# Revit family: ASH_Contour21_Multiproduct_S6360;S6361
name_source: partatom
category: Plumbing Fixtures
revit_build: Autodesk Revit MEP 2014 (Build: 20130308_1515(x64)
units: mm (PartAtom-declared; Revit-internal decimal feet)

## types (10) — shared parameters
AccessibilityPerformance = Part-M
Accessories = www.idealspec.co.uk
AreaUnits = millimeters
Assembly Code = C1030200
AssetType = Fixed
Brand = Armitage Shanks
ConnectionType = Plumbing
Default Elevation = 680 mm  [stored 2.23097 ft]
DurationUnit = year
ExpectedLife = 30
Finish = Chrome
IfcExportAs = IfcValveType
IfcExportType = FAUCET
InstallationInstructions = www.idealspec.co.uk/resources.html
LinearUnits = millimeters
ManufacturerURL = www.idealspec.co.uk
Material = Aluminium
NBSDescription = Support rails
NBSReference = 45-35-70/360
NominalHeight = 242 mm
NominalWidth = 107 mm
Shape = Sculptured
Size = 0 x 0 x 0 mm
Space = Internal
SpareParts = www.fastpart-spares.co.uk
URL = www.idealspec.co.uk
Uniclass2015Code = Pr_40_20_76_84
Uniclass2015Title = Support rails
Uniclass2015Version = Products v1.1
Version = 1
VolumeUnits = Litres
WarrantyDescription = Manufacturers Warranty
WarrantyDurationParts = 5
WarrantyDurationUnit = year
zero-valued in all types: CWFU, Cost, HWFU, WFU

## per-type parameters (varying)
| type | BIMObjectName | BarCode | Color | Description | Features | GrabRailMtl | Model | ModelNumber | ModelReference | Name | NettWeight | NominalLength | ProductInformation |
| S6360AC - Contour21 Support Rail 800 x 350mm - Doc M Compliant - White | ASH_ArmitageShanks_SupportRails_Contour21_S6360AC | 5017830444909 | White | Contour 21 hinged support rail 80 x 35mm diameter, doc m compliant | Hinged support rail 80 x 35mm diameter, doc m compliant | ASH_ArmitageShanks_Brassware_White_AC_Render | S6360AC | S6360AC | Contour 21 hinged support rail 80 x 35mm diameter, doc m compliant | SupportRails_Contour21_S6360AC_ArmitageShanks | 3.15 Kg | 800 mm | www.idealspec.co.uk/assets/datasheet/S6360AC |
| S6361AC - Contour21 Support Rail 650 x 350mm - NHS HTM64 - White | ASH_ArmitageShanks_SupportRails_Contour21_S6361AC | 5017830444954 | White | Contour 21 hinged support rail nhs htm64 projection 65 x 35mm diameter | Hinged support rail nhs htm64 projection 65 x 35mm diameter | ASH_ArmitageShanks_Brassware_White_AC_Render | S6361AC | S6361AC | Contour 21 hinged support rail nhs htm64 projection 65 x 35mm diameter | SupportRails_Contour21_S6361AC_ArmitageShanks | 3 Kg | 650 mm  [stored 2.13255 ft] | www.idealspec.co.uk/assets/datasheet/S6361AC |
| S636036 - Contour21 Support Rail 800 x 350mm - Doc M Compliant - Blue | ASH_ArmitageShanks_SupportRails_Contour21_S636036 | 5017830444893 | Blue | Contour 21 hinged support rail 80 x 35mm diameter, doc m compliant | Hinged support rail 80 x 35mm diameter, doc m compliant | ASH_ArmitageShanks_Brassware_Blue_36_Render | S636036 | S636036 | Contour 21 hinged support rail 80 x 35mm diameter, doc m compliant | SupportRails_Contour21_S636036_ArmitageShanks | 3.15 Kg | 800 mm | www.idealspec.co.uk/assets/datasheet/S636036 |
| S6360RN - Contour21 Support Rail 800 x 350mm - Doc M Compliant - Charcoal | ASH_ArmitageShanks_SupportRails_Contour21_S6360RN | 5017830444930 | Charcoal | Contour 21 hinged support rail 80 x 35mm diameter, doc m compliant | Hinged support rail 80 x 35mm diameter, doc m compliant | ASH_ArmitageShanks_Brassware_Charcoal_RN_Render | S6360RN | S6360RN | Contour 21 hinged support rail 80 x 35mm diameter, doc m compliant | SupportRails_Contour21_S6360RN_ArmitageShanks | 3.15 Kg | 800 mm | www.idealspec.co.uk/assets/datasheet/S6360RN |
| S6360LJ - Contour21 Support Rail 800 x 350mm - Doc M Compliant - Light Grey | ASH_ArmitageShanks_SupportRails_Contour21_S6360LJ | 5017830444916 | Grey | Contour 21 hinged support rail 80 x 35mm diameter, doc m compliant | Hinged support rail 80 x 35mm diameter, doc m compliant | ASH_ArmitageShanks_Brassware_LightGrey_LJ_Render | S6360LJ | S6360LJ | Contour 21 hinged support rail 80 x 35mm diameter, doc m compliant | SupportRails_Contour21_S6360LJ_ArmitageShanks | 3.15 Kg | 800 mm | www.idealspec.co.uk/assets/datasheet/S6360LJ |
| S6360MY - Contour21 Support Rail 800 x 350mm - Doc M Compliant - Satinless Steel | ASH_ArmitageShanks_SupportRails_Contour21_S6360MY | 5017830444923 | Stainless Steel finish | Contour 21 hinged support rail 80 x 35mm diameter, doc m compliant | Hinged support rail 80 x 35mm diameter, doc m compliant | ASH_ArmitageShanks_Brassware_Steel_MY_Render | S6360MY | S6360MY | Contour 21 hinged support rail 80 x 35mm diameter, doc m compliant | SupportRails_Contour21_S6360MY_ArmitageShanks | 3.15 Kg | 800 mm | www.idealspec.co.uk/assets/datasheet/S6360MY |
| S636136 - Contour21 Support Rail 650 x 350mm - NHS HTM64 - Blue | ASH_ArmitageShanks_SupportRails_Contour21_S636136 | 5017830444947 | Blue | Contour 21 hinged support rail nhs htm64 projection 65 x 35mm diameter | Hinged support rail nhs htm64 projection 65 x 35mm diameter | ASH_ArmitageShanks_Brassware_Blue_36_Render | S636136 | S636136 | Contour 21 hinged support rail nhs htm64 projection 65 x 35mm diameter | SupportRails_Contour21_S636136_ArmitageShanks | 3 Kg | 650 mm  [stored 2.13255 ft] | www.idealspec.co.uk/assets/datasheet/S636136 |
| S6361RN - Contour21 Support Rail 650 x 350mm - NHS HTM64 - Charcoal | ASH_ArmitageShanks_SupportRails_Contour21_S6361RN | 5017830444985 | Charcoal | Contour 21 hinged support rail nhs htm64 projection 65 x 35mm diameter | Hinged support rail nhs htm64 projection 65 x 35mm diameter | ASH_ArmitageShanks_Brassware_Charcoal_RN_Render | S6361RN | S6361RN | Contour 21 hinged support rail nhs htm64 projection 65 x 35mm diameter | SupportRails_Contour21_S6361RN_ArmitageShanks | 3 Kg | 650 mm  [stored 2.13255 ft] | www.idealspec.co.uk/assets/datasheet/S6361RN |
| S6361LJ - Contour21 Support Rail 650 x 350mm - NHS HTM64 - Light Grey | ASH_ArmitageShanks_SupportRails_Contour21_S6361LJ | 5017830444961 | Grey | Contour 21 hinged support rail nhs htm64 projection 65 x 35mm diameter | Hinged support rail nhs htm64 projection 65 x 35mm diameter | ASH_ArmitageShanks_Brassware_LightGrey_LJ_Render | S6361LJ | S6361LJ | Contour 21 hinged support rail nhs htm64 projection 65 x 35mm diameter | SupportRails_Contour21_S6361LJ_ArmitageShanks | 3 Kg | 650 mm  [stored 2.13255 ft] | www.idealspec.co.uk/assets/datasheet/S6361LJ |
| S6361MY - Contour21 Support Rail 650 x 350mm - NHS HTM64 - Stainless Steel | ASH_ArmitageShanks_SupportRails_Contour21_S6361MY | 5017830444978 | Stainless Steel finish | Contour 21 hinged support rail nhs htm64 projection 65 x 35mm diameter | Hinged support rail nhs htm64 projection 65 x 35mm diameter | ASH_ArmitageShanks_Brassware_Steel_MY_Render | S6361MY | S6361MY | Contour 21 hinged support rail nhs htm64 projection 65 x 35mm diameter | SupportRails_Contour21_S6361MY_ArmitageShanks | 3 Kg | 650 mm  [stored 2.13255 ft] | www.idealspec.co.uk/assets/datasheet/S6361MY |

note: [stored X ft] marks values corroborated as IEEE doubles in the binary element streams (Revit-internal decimal feet)

## geometry (parser evidence)
native form markers: Sweep x6
no freeform markers — native parametric forms only
